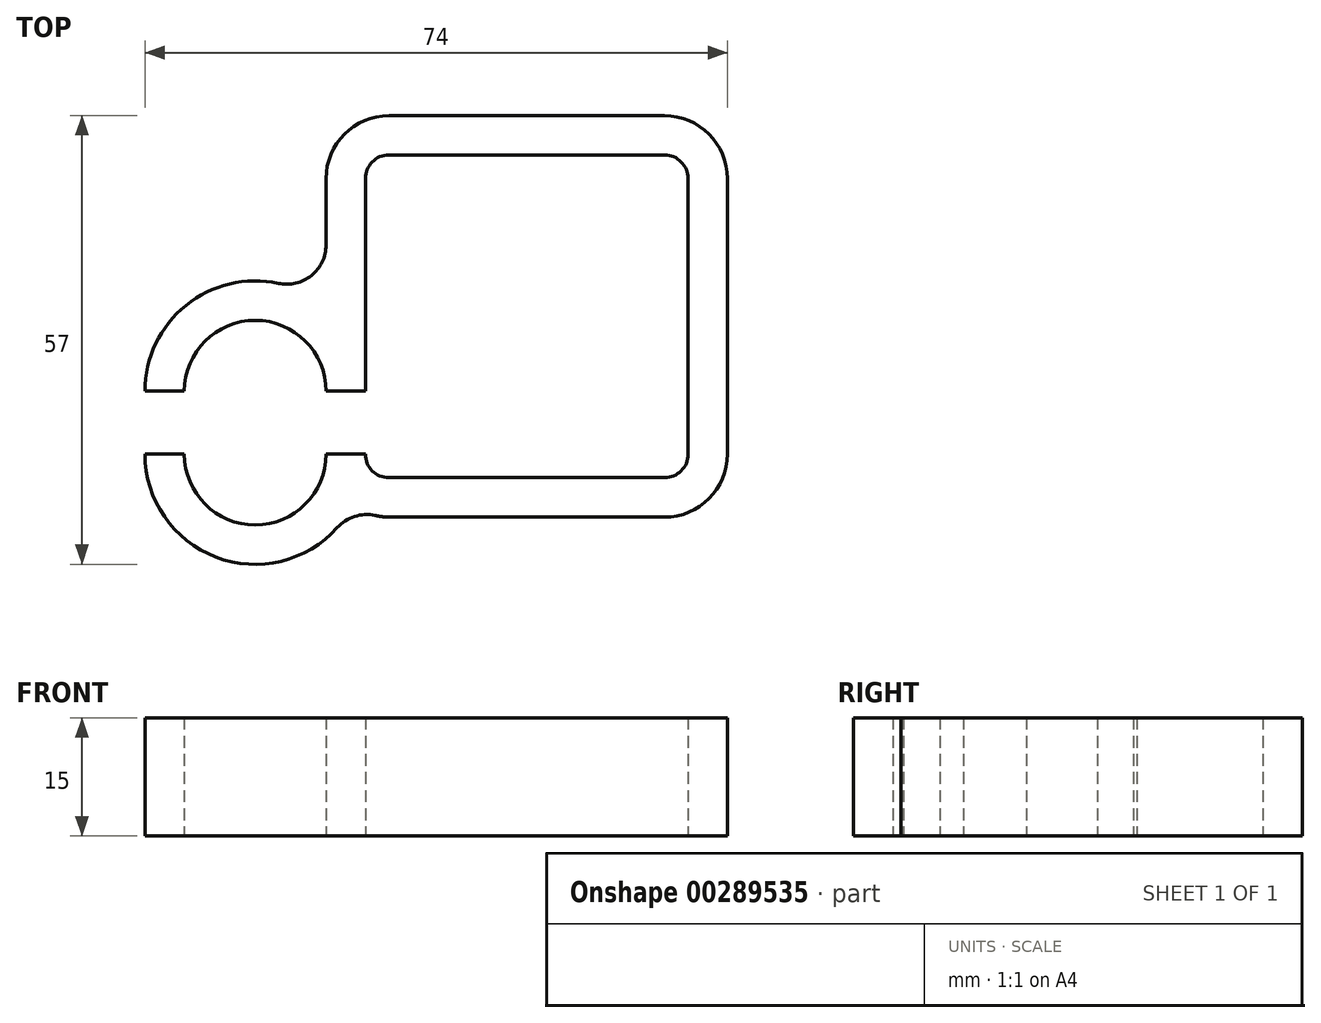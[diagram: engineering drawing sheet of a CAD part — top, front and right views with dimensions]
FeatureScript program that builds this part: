
annotation { "Feature Type Name" : "Feature", "Feature Type Description" : "" }
export const myFeature = defineFeature(function(context is Context, id is Id, definition is map)
    precondition{}
    {
        {
            var Q0;
            Q0=qCreatedBy(makeId("Top.planeOp"),FACE);
            var sketch = newSketch(context, id + "F0", { "sketchPlane" : qUnion([Q0])});
            skLineSegment(sketch, "E0.bottom", {"start": v(17.5, -20.5) * mm, "end": v(-17.5, -20.5) * mm});
            skLineSegment(sketch, "E0.top", {"start": v(17.5, 20.5) * mm, "end": v(-17.5, 20.5) * mm});
            skLineSegment(sketch, "E0.left", {"start": v(20.5, -17.5) * mm, "end": v(20.5, 17.5) * mm});
            skLineSegment(sketch, "E0.right", {"start": v(-20.5, -9.5) * mm, "end": v(-20.5, 17.5) * mm});
            skPoint(sketch, "E0.middle", {"position": v(0, 0) * mm});
            skPoint(sketch, "E1.visualSharp", {"position": v(-20.5, 20.5) * mm});
            skArc(sketch, "E1.filletArc", {"start": v(-17.5, 20.5) * mm, "mid": v(-19.62, 19.62) * mm, "end": v(-20.5, 17.5) * mm});
            skPoint(sketch, "E2.visualSharp", {"position": v(20.5, 20.5) * mm});
            skArc(sketch, "E2.filletArc", {"start": v(20.5, 17.5) * mm, "mid": v(19.62, 19.62) * mm, "end": v(17.5, 20.5) * mm});
            skPoint(sketch, "E3.visualSharp", {"position": v(20.5, -20.5) * mm});
            skArc(sketch, "E3.filletArc", {"start": v(17.5, -20.5) * mm, "mid": v(19.62, -19.62) * mm, "end": v(20.5, -17.5) * mm});
            skPoint(sketch, "E4.visualSharp", {"position": v(-20.5, -20.5) * mm});
            skArc(sketch, "E4.filletArc", {"start": v(-20.5, -17.5) * mm, "mid": v(-19.62, -19.62) * mm, "end": v(-17.5, -20.5) * mm});
            skArc(sketch, "E5.0", {"start": v(25.5, 17.5) * mm, "mid": v(23.16, 23.16) * mm, "end": v(17.5, 25.5) * mm});
            skLineSegment(sketch, "E5.1", {"start": v(25.5, -17.5) * mm, "end": v(25.5, 17.5) * mm});
            skLineSegment(sketch, "E5.2", {"start": v(17.5, 25.5) * mm, "end": v(-17.5, 25.5) * mm});
            skArc(sketch, "E5.3", {"start": v(17.5, -25.5) * mm, "mid": v(23.16, -23.16) * mm, "end": v(25.5, -17.5) * mm});
            skArc(sketch, "E5.4", {"start": v(-17.5, 25.5) * mm, "mid": v(-23.16, 23.16) * mm, "end": v(-25.5, 17.5) * mm});
            skLineSegment(sketch, "E5.5", {"start": v(-25.5, 9.07) * mm, "end": v(-25.5, 17.5) * mm});
            skArc(sketch, "E5.6", {"start": v(-19.26, -25.3) * mm, "mid": v(-18.38, -25.45) * mm, "end": v(-17.5, -25.5) * mm});
            skLineSegment(sketch, "E5.7", {"start": v(17.5, -25.5) * mm, "end": v(-17.5, -25.5) * mm});
            skLineSegment(sketch, "E6", {"start": v(-20.5, -17.5) * mm, "end": v(-25.5, -17.5) * mm});
            skLineSegment(sketch, "E7", {"start": v(-25.5, -9.5) * mm, "end": v(-20.5, -9.5) * mm});
            skArc(sketch, "E8", {"start": v(-25.5, -9.5) * mm, "mid": v(-34.5, -0.5) * mm, "end": v(-43.5, -9.5) * mm});
            skArc(sketch, "E9.0", {"start": v(-31.55, 4.19) * mm, "mid": v(-43.3, 1.4) * mm, "end": v(-48.5, -9.5) * mm});
            skLineSegment(sketch, "E10", {"start": v(-48.5, -9.5) * mm, "end": v(-43.5, -9.5) * mm});
            skLineSegment(sketch, "E11", {"start": v(-20.5, -9.5) * mm, "end": v(-20.5, -17.5) * mm, "construction": true});
            skLineSegment(sketch, "E12", {"start": v(-20.5, -13.5) * mm, "end": v(-55.92, -13.5) * mm, "construction": true});
            skLineSegment(sketch, "E13.MirrorCS", {"start": v(-48.5, -17.5) * mm, "end": v(-43.5, -17.5) * mm});
            skArc(sketch, "E14.MirrorCS", {"start": v(-25.5, -17.5) * mm, "mid": v(-34.5, -26.5) * mm, "end": v(-43.5, -17.5) * mm});
            skArc(sketch, "E15.MirrorCS", {"start": v(-24.08, -26.85) * mm, "mid": v(-39.5, -30.58) * mm, "end": v(-48.5, -17.5) * mm});
            skPoint(sketch, "E16.orphan", {"position": v(-20.5, -9.5) * mm});
            skPoint(sketch, "E17.orphan", {"position": v(-20.5, -17.5) * mm});
            skPoint(sketch, "E18.visualSharp", {"position": v(-25.5, 1.22) * mm});
            skArc(sketch, "E18.filletArc", {"start": v(-31.55, 4.19) * mm, "mid": v(-27.36, 5.18) * mm, "end": v(-25.5, 9.07) * mm});
            skPoint(sketch, "E19.visualSharp", {"position": v(-22.12, -24.03) * mm});
            skArc(sketch, "E19.filletArc", {"start": v(-19.26, -25.3) * mm, "mid": v(-21.88, -25.42) * mm, "end": v(-24.08, -26.85) * mm});
            skSolve(sketch);
        }
        {
            var Q0;
            Q0 = qSketchRegion(id + "F0", true);
            extrude(context, id + "F1", {"entities" : qUnion([Q0]), "depth" : 15 * mm});
        }
    });
